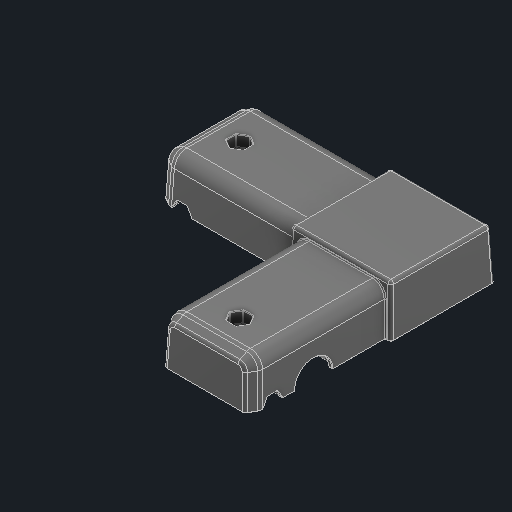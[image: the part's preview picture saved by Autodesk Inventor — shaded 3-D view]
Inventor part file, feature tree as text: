
AUTODESK INVENTOR PART (.ipt)
format: ipt  version: 2024.2 (Build 282272000, 272)  size: 5,282,816 bytes
history: native  units: in
note: dims shown in document units (in); Inventor stores cm internally (conversion verified against a paired STEP export)
features: fillet x1
ambient origin geometry x8: Origin, YZ Plane, XZ Plane, XY Plane, X Axis, Y Axis, Z Axis, Center Point
bodies: Solid1 (feature_tree)
feature tree (1):
  fillet  "Fillet54"  [1 undecoded]
note: 1 required parameter value undecoded (feature->parameter linkage not recoverable at this tier; creation-order binding heuristic only, values carry confidence <= 0.55)
